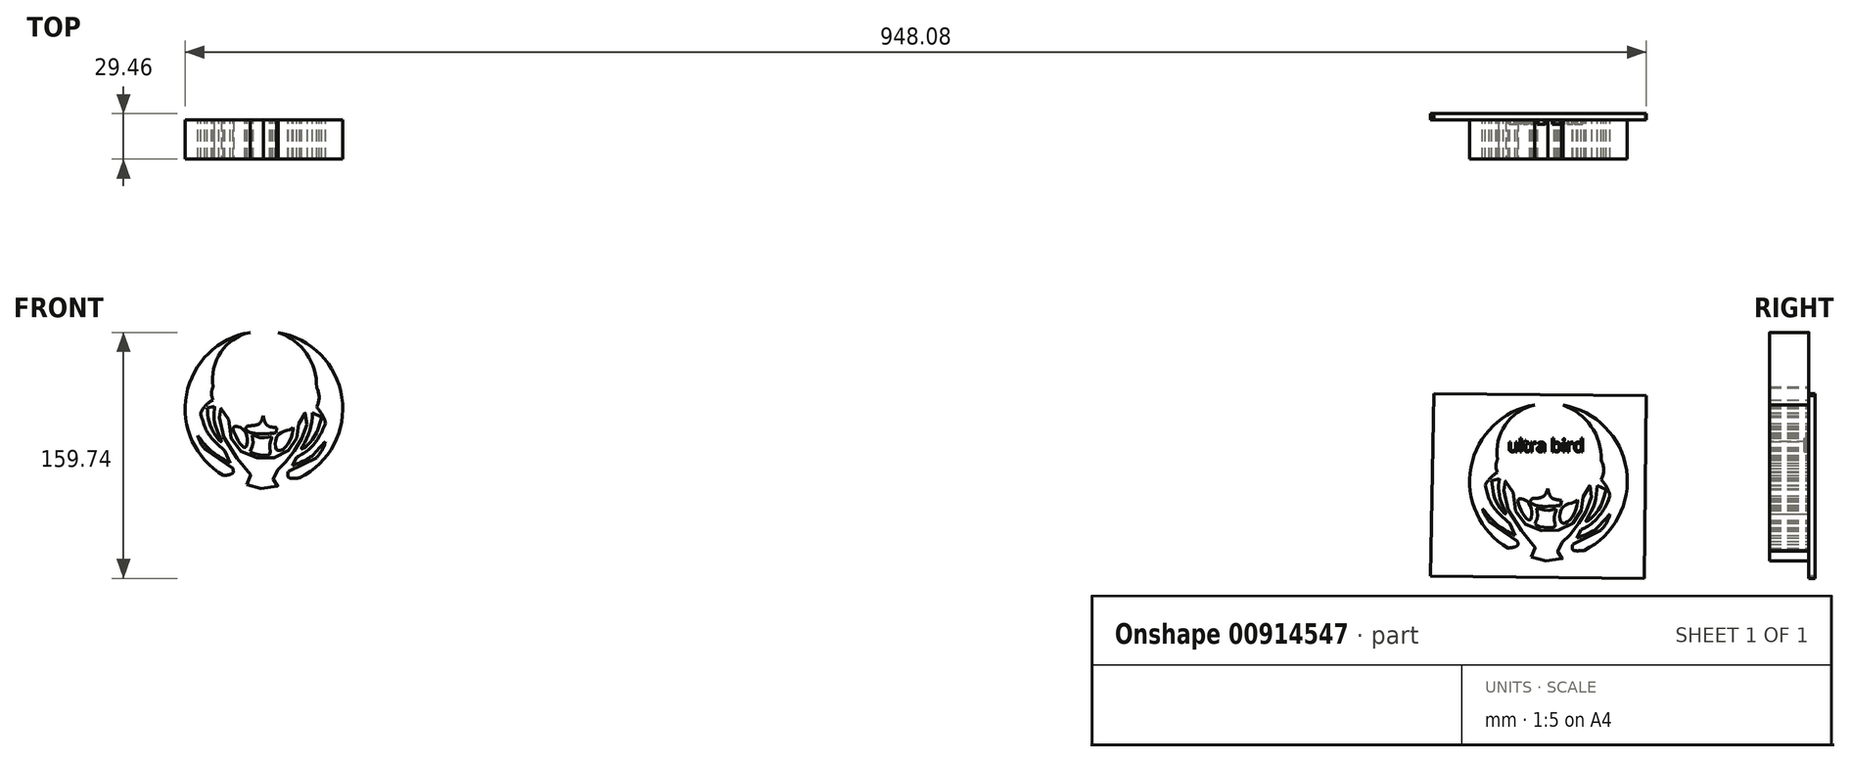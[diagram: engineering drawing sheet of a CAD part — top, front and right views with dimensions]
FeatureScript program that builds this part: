
annotation { "Feature Type Name" : "Feature", "Feature Type Description" : "" }
export const myFeature = defineFeature(function(context is Context, id is Id, definition is map)
    precondition{}
    {
        {
            var Q0;
            Q0=qCreatedBy(makeId("Front.planeOp"),FACE);
            var sketch = newSketch(context, id + "F0", { "sketchPlane" : qUnion([Q0])});
            skArc(sketch, "E0", {"start": v(-5.77, 42.62) * mm, "mid": v(-24.76, 29.64) * mm, "end": v(-29.8, 7.2) * mm});
            skArc(sketch, "E1", {"start": v(-29.8, 7.2) * mm, "mid": v(-30.8, 2.99) * mm, "end": v(-29.8, -1.22) * mm});
            skArc(sketch, "E2", {"start": v(-29.8, -1.22) * mm, "mid": v(-40.01, -15.91) * mm, "end": v(-35.08, -33.12) * mm});
            skArc(sketch, "E3", {"start": v(-5.77, 42.62) * mm, "mid": v(-47, 2.18) * mm, "end": v(-23, -50.35) * mm});
            skLineSegment(sketch, "E4", {"start": v(-35.08, -33.12) * mm, "end": v(-16.9, -45.88) * mm});
            skFitSpline(sketch, "E5", {"points": [v(-16.9, -45.88) * mm, v(-16.9, -48.73) * mm, v(-23, -50.35) * mm], "startDerivative": vector(2.05, -7.97) * mm, "endDerivative": vector(-13.26, -1.41) * mm});
            skArc(sketch, "E6", {"start": v(37.4, 6.65) * mm, "mid": v(30.96, 28.72) * mm, "end": v(12.55, 42.48) * mm});
            skArc(sketch, "E7", {"start": v(37.4, -5.84) * mm, "mid": v(39.04, 0.4) * mm, "end": v(37.4, 6.65) * mm});
            skArc(sketch, "E8", {"start": v(37.4, -38.68) * mm, "mid": v(43.92, -22.26) * mm, "end": v(37.4, -5.84) * mm});
            skArc(sketch, "E9", {"start": v(26.4, -51.85) * mm, "mid": v(53.85, 0.36) * mm, "end": v(12.55, 42.48) * mm});
            skLineSegment(sketch, "E10", {"start": v(37.4, -38.68) * mm, "end": v(19.07, -47.78) * mm});
            skFitSpline(sketch, "E11", {"points": [v(19.07, -47.78) * mm, v(19.07, -51.44) * mm, v(26.4, -51.85) * mm], "startDerivative": vector(-2.59, -10.54) * mm, "endDerivative": vector(16.17, 1.7) * mm});
            skFitSpline(sketch, "E12", {"points": [v(-7.8, -56.2) * mm, v(-5.23, -51.85) * mm, v(-18.66, -33.39) * mm, v(-25.72, -12.35) * mm, v(-25.18, -6.79) * mm, v(-20.43, -11.67) * mm, v(-17.58, -28.1) * mm, v(-7.13, -37.19) * mm, v(7.94, -39.09) * mm, v(19.07, -34.07) * mm, v(25.04, -24.57) * mm, v(26.4, -14.66) * mm, v(30.6, -9.9) * mm, v(30.74, -19.33) * mm, v(26.4, -28.77) * mm, v(20.56, -37.73) * mm, v(14.73, -44.25) * mm, v(11.2, -47.78) * mm, v(9.3, -52.93) * mm, v(12.55, -56.33) * mm, v(4.68, -58.77) * mm, v(-7.8, -56.2) * mm]});
            skFitSpline(sketch, "E13", {"points": [v(-5.5, -34.6) * mm, v(-3.87, -30) * mm, v(-4.28, -24.43) * mm, v(1.56, -25.92) * mm, v(8.21, -25.24) * mm, v(6.99, -29.86) * mm, v(7.26, -36.24) * mm, v(0, -36.78) * mm, v(-5.5, -34.6) * mm]});
            skFitSpline(sketch, "E14", {"points": [v(22.06, -19.14) * mm, v(19.98, -28.1) * mm, v(11.88, -33.93) * mm, v(12.42, -24.02) * mm, v(20.97, -20.09) * mm, v(22.06, -19.14) * mm]});
            skFitSpline(sketch, "E15", {"points": [v(-15.4, -18.46) * mm, v(-8.75, -22.26) * mm, v(-9.16, -32.17) * mm, v(-16.63, -20.5) * mm, v(-15.4, -18.46) * mm]});
            skFitSpline(sketch, "E16", {"points": [v(-28.7, -5.43) * mm, v(-28.16, -18.05) * mm, v(-24.5, -28.37) * mm, v(-30.33, -20.77) * mm, v(-33.6, -6.51) * mm], "startDerivative": vector(-4.9, -45.08) * mm, "endDerivative": vector(-4.2, 50.81) * mm});
            skLineSegment(sketch, "E17", {"start": v(-33.6, -6.51) * mm, "end": v(-28.7, -5.43) * mm});
            skFitSpline(sketch, "E18", {"points": [v(-37.84, -9.5) * mm, v(-33.17, -22.59) * mm, v(-22.02, -34.3) * mm], "startDerivative": vector(6.84, -28.3) * mm, "endDerivative": vector(24.54, -21.35) * mm});
            skFitSpline(sketch, "E19", {"points": [v(-39.63, -24.55) * mm, v(-30.78, -34.48) * mm, v(-18.5, -42.2) * mm], "startDerivative": vector(16.64, -21.56) * mm, "endDerivative": vector(25.53, -13.79) * mm});
            skLineSegment(sketch, "E20", {"start": v(-22.02, -34.3) * mm, "end": v(-18.5, -42.2) * mm});
            skFitSpline(sketch, "E21", {"points": [v(2.8, -11.62) * mm, v(5.15, -17.52) * mm, v(11.64, -19.33) * mm], "startDerivative": vector(2.81, -14.05) * mm, "endDerivative": vector(14.82, -1.42) * mm});
            skFitSpline(sketch, "E22", {"points": [v(-9, -20.27) * mm, v(-6.39, -22.04) * mm, v(-2.33, -23.14) * mm, v(4.84, -23.17) * mm, v(11.17, -22.61) * mm, v(11.2, -22.57) * mm], "startDerivative": vector(12.7, -10) * mm, "endDerivative": vector(0.5, 1.58) * mm});
            skFitSpline(sketch, "E23", {"points": [v(2.8, -11.62) * mm, v(0, -16.8) * mm, v(-7.4, -18.07) * mm], "startDerivative": vector(-4.08, -13.06) * mm, "endDerivative": vector(-16.07, -0.1) * mm});
            skLineSegment(sketch, "E24", {"start": v(-7.4, -18.07) * mm, "end": v(-9, -20.27) * mm});
            skLineSegment(sketch, "E25", {"start": v(11.64, -19.33) * mm, "end": v(11.2, -22.57) * mm});
            skFitSpline(sketch, "E26", {"points": [v(34.82, -9.7) * mm, v(31.9, -24.57) * mm, v(27.6, -33.08) * mm, v(30.26, -31.6) * mm, v(35.23, -26.1) * mm, v(38.18, -20.68) * mm, v(40.65, -12.4) * mm], "startDerivative": vector(-4.6, -64.2) * mm, "endDerivative": vector(13.18, 50.57) * mm});
            skLineSegment(sketch, "E27", {"start": v(34.82, -9.7) * mm, "end": v(40.65, -12.4) * mm});
            skFitSpline(sketch, "E28", {"points": [v(43.2, -16.46) * mm, v(37.69, -27.41) * mm, v(28.9, -36.06) * mm, v(24.49, -38.33) * mm, v(24.4, -38.41) * mm], "startDerivative": vector(-12.8, -30.73) * mm, "endDerivative": vector(-1.12, -2.02) * mm});
            skFitSpline(sketch, "E29", {"points": [v(43.16, -28.2) * mm, v(36.3, -35.71) * mm, v(34.3, -37.73) * mm, v(28.47, -41.1) * mm, v(21.55, -43.86) * mm], "startDerivative": vector(-26, -28.15) * mm, "endDerivative": vector(-25.57, -9.24) * mm});
            skLineSegment(sketch, "E30", {"start": v(24.42, -38.39) * mm, "end": v(21.55, -43.86) * mm});
            skArc(sketch, "E31", {"start": v(-839.27, 89.75) * mm, "mid": v(-858.27, 76.77) * mm, "end": v(-863.3, 54.33) * mm});
            skArc(sketch, "E32", {"start": v(-863.3, 54.33) * mm, "mid": v(-864.3, 50.12) * mm, "end": v(-863.3, 45.91) * mm});
            skArc(sketch, "E33", {"start": v(-863.3, 45.91) * mm, "mid": v(-873.52, 31.22) * mm, "end": v(-868.59, 14.02) * mm});
            skArc(sketch, "E34", {"start": v(-839.27, 89.75) * mm, "mid": v(-880.51, 49.31) * mm, "end": v(-856.5, -3.22) * mm});
            skLineSegment(sketch, "E35", {"start": v(-868.59, 14.02) * mm, "end": v(-850.4, 1.26) * mm});
            skFitSpline(sketch, "E36", {"points": [v(-850.4, 1.26) * mm, v(-850.4, -1.6) * mm, v(-856.5, -3.22) * mm], "startDerivative": vector(2.05, -7.97) * mm, "endDerivative": vector(-13.26, -1.41) * mm});
            skArc(sketch, "E37", {"start": v(-796.1, 53.78) * mm, "mid": v(-802.54, 75.85) * mm, "end": v(-820.95, 89.61) * mm});
            skArc(sketch, "E38", {"start": v(-796.1, 41.3) * mm, "mid": v(-794.46, 47.54) * mm, "end": v(-796.1, 53.78) * mm});
            skArc(sketch, "E39", {"start": v(-796.1, 8.45) * mm, "mid": v(-789.59, 24.87) * mm, "end": v(-796.1, 41.3) * mm});
            skArc(sketch, "E40", {"start": v(-807.1, -4.71) * mm, "mid": v(-779.65, 47.5) * mm, "end": v(-820.95, 89.61) * mm});
            skLineSegment(sketch, "E41", {"start": v(-796.1, 8.45) * mm, "end": v(-814.43, -0.64) * mm});
            skFitSpline(sketch, "E42", {"points": [v(-814.43, -0.64) * mm, v(-814.43, -4.3) * mm, v(-807.1, -4.71) * mm], "startDerivative": vector(-2.59, -10.54) * mm, "endDerivative": vector(16.17, 1.7) * mm});
            skFitSpline(sketch, "E43", {"points": [v(-841.3, -9.06) * mm, v(-838.73, -4.71) * mm, v(-852.16, 13.74) * mm, v(-859.22, 34.78) * mm, v(-858.68, 40.35) * mm, v(-853.93, 35.46) * mm, v(-851.08, 19.04) * mm, v(-840.63, 9.94) * mm, v(-825.56, 8.04) * mm, v(-814.43, 13.07) * mm, v(-808.46, 22.57) * mm, v(-807.1, 32.47) * mm, v(-802.9, 37.22) * mm, v(-802.76, 27.8) * mm, v(-807.1, 18.36) * mm, v(-812.94, 9.4) * mm, v(-818.77, 2.89) * mm, v(-822.3, -0.64) * mm, v(-824.2, -5.8) * mm, v(-820.95, -9.2) * mm, v(-828.82, -11.64) * mm, v(-841.3, -9.06) * mm]});
            skFitSpline(sketch, "E44", {"points": [v(-839, 12.52) * mm, v(-837.37, 17.14) * mm, v(-837.78, 22.7) * mm, v(-831.94, 21.2) * mm, v(-825.29, 21.89) * mm, v(-826.51, 17.27) * mm, v(-826.24, 10.9) * mm, v(-833.5, 10.35) * mm, v(-839, 12.52) * mm]});
            skFitSpline(sketch, "E45", {"points": [v(-811.45, 28) * mm, v(-813.52, 19.04) * mm, v(-821.62, 13.2) * mm, v(-821.08, 23.1) * mm, v(-812.53, 27.04) * mm, v(-811.45, 28) * mm]});
            skFitSpline(sketch, "E46", {"points": [v(-848.9, 28.67) * mm, v(-842.26, 24.87) * mm, v(-842.66, 14.97) * mm, v(-850.13, 26.64) * mm, v(-848.9, 28.67) * mm]});
            skFitSpline(sketch, "E47", {"points": [v(-862.2, 41.7) * mm, v(-861.66, 29.08) * mm, v(-858, 18.77) * mm, v(-863.84, 26.37) * mm, v(-867.1, 40.62) * mm], "startDerivative": vector(-4.9, -45.08) * mm, "endDerivative": vector(-4.2, 50.81) * mm});
            skLineSegment(sketch, "E48", {"start": v(-867.1, 40.62) * mm, "end": v(-862.2, 41.7) * mm});
            skFitSpline(sketch, "E49", {"points": [v(-871.34, 37.62) * mm, v(-866.67, 24.54) * mm, v(-855.52, 12.84) * mm], "startDerivative": vector(6.84, -28.3) * mm, "endDerivative": vector(24.54, -21.35) * mm});
            skFitSpline(sketch, "E50", {"points": [v(-873.13, 22.58) * mm, v(-864.28, 12.66) * mm, v(-852.01, 4.94) * mm], "startDerivative": vector(16.64, -21.56) * mm, "endDerivative": vector(25.53, -13.79) * mm});
            skLineSegment(sketch, "E51", {"start": v(-855.52, 12.84) * mm, "end": v(-852.01, 4.94) * mm});
            skFitSpline(sketch, "E52", {"points": [v(-830.7, 35.51) * mm, v(-828.35, 29.61) * mm, v(-821.86, 27.8) * mm], "startDerivative": vector(2.81, -14.05) * mm, "endDerivative": vector(14.82, -1.42) * mm});
            skFitSpline(sketch, "E53", {"points": [v(-842.5, 26.86) * mm, v(-839.89, 25.1) * mm, v(-835.83, 23.99) * mm, v(-828.66, 23.97) * mm, v(-822.33, 24.52) * mm, v(-822.3, 24.56) * mm], "startDerivative": vector(12.7, -10) * mm, "endDerivative": vector(0.5, 1.58) * mm});
            skFitSpline(sketch, "E54", {"points": [v(-830.7, 35.51) * mm, v(-833.5, 30.33) * mm, v(-840.9, 29.06) * mm], "startDerivative": vector(-4.08, -13.06) * mm, "endDerivative": vector(-16.07, -0.1) * mm});
            skLineSegment(sketch, "E55", {"start": v(-840.9, 29.06) * mm, "end": v(-842.5, 26.86) * mm});
            skLineSegment(sketch, "E56", {"start": v(-821.86, 27.8) * mm, "end": v(-822.3, 24.56) * mm});
            skFitSpline(sketch, "E57", {"points": [v(-798.68, 37.43) * mm, v(-801.6, 22.56) * mm, v(-805.9, 14.05) * mm, v(-803.24, 15.52) * mm, v(-798.27, 21.03) * mm, v(-795.32, 26.45) * mm, v(-792.85, 34.72) * mm], "startDerivative": vector(-4.6, -64.2) * mm, "endDerivative": vector(13.18, 50.57) * mm});
            skLineSegment(sketch, "E58", {"start": v(-798.68, 37.43) * mm, "end": v(-792.85, 34.72) * mm});
            skFitSpline(sketch, "E59", {"points": [v(-790.3, 30.68) * mm, v(-795.81, 19.72) * mm, v(-804.6, 11.07) * mm, v(-809.01, 8.8) * mm, v(-809.1, 8.72) * mm], "startDerivative": vector(-12.8, -30.73) * mm, "endDerivative": vector(-1.12, -2.02) * mm});
            skFitSpline(sketch, "E60", {"points": [v(-790.34, 18.93) * mm, v(-797.2, 11.42) * mm, v(-799.2, 9.4) * mm, v(-805.03, 6.04) * mm, v(-811.95, 3.28) * mm], "startDerivative": vector(-26, -28.15) * mm, "endDerivative": vector(-25.57, -9.24) * mm});
            skLineSegment(sketch, "E61", {"start": v(-809.08, 8.74) * mm, "end": v(-811.95, 3.28) * mm});
            skSolve(sketch);
        }
        {
            var Q0;
            Q0 = qSketchRegion(id + "F0", true);
            extrude(context, id + "F1", {"entities" : qUnion([Q0]), "depth" : 25.4 * mm, "offsetDistance" : 25.4 * mm});
        }
        {
            var Q0;
            Q0=qCreatedBy(makeId("Front.planeOp"),FACE);
            var sketch = newSketch(context, id + "F2", { "sketchPlane" : qUnion([Q0])});
            skLineSegment(sketch, "E62", {"start": v(-71.2, 50.02) * mm, "end": v(66.73, 48.5) * mm});
            skLineSegment(sketch, "E63", {"start": v(66.73, 48.5) * mm, "end": v(65.42, -70) * mm});
            skLineSegment(sketch, "E64", {"start": v(65.42, -70) * mm, "end": v(-73.32, -68.47) * mm});
            skLineSegment(sketch, "E65", {"start": v(-73.32, -68.47) * mm, "end": v(-71.2, 50.02) * mm});
            skSolve(sketch);
        }
        {
            var Q0;
            Q0 = qSketchRegion(id + "F2", true);
            extrude(context, id + "F3", {"entities" : qUnion([Q0]), "oppositeDirection" : true, "depth" : 4.06 * mm, "offsetDistance" : 25.4 * mm});
        }
        {
            var Q0;
            Q0=qCreatedBy(makeId("Front.planeOp"),FACE);
            var sketch = newSketch(context, id + "F4", { "sketchPlane" : qUnion([Q0])});
            skText(sketch, "E66", { "text": "ultra bird\n\n", "fontName": "OpenSans-Regular.ttf"});
            const initialGuessF4  = {"E66": [-0.02322, 0.01224, 1, 0, 0.00825]};
            skSetInitialGuess(sketch, initialGuessF4);
            skSolve(sketch);
        }
        {
            var Q0;
            Q0 = qSketchRegion(id + "F4", true);
            extrude(context, id + "F5", {"entities" : qUnion([Q0]), "operationType" : NewBodyOperationType.ADD, "depth" : 2.8 * mm, "offsetDistance" : 25.4 * mm});
        }
    });
